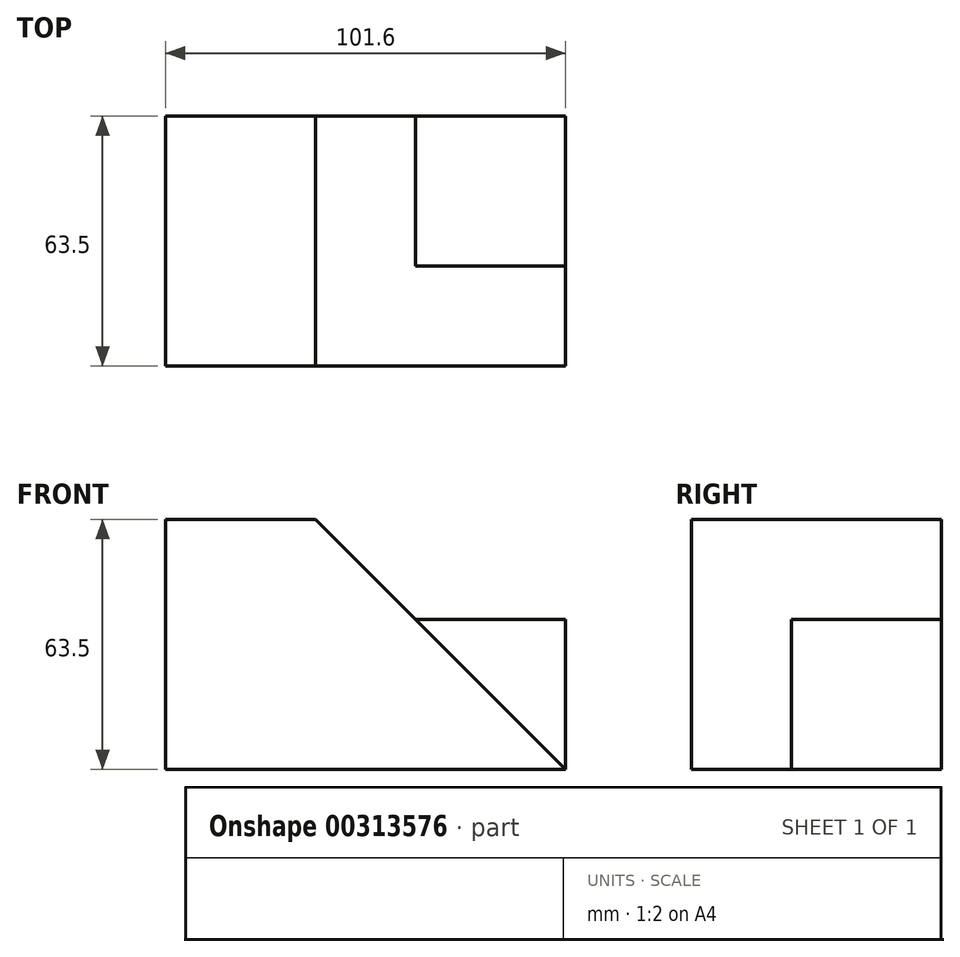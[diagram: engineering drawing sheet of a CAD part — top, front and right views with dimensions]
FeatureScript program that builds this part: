
annotation { "Feature Type Name" : "Feature", "Feature Type Description" : "" }
export const myFeature = defineFeature(function(context is Context, id is Id, definition is map)
    precondition{}
    {
        {
            var Q0;
            Q0=qCreatedBy(makeId("Front.planeOp"),FACE);
            var sketch = newSketch(context, id + "F0", { "sketchPlane" : qUnion([Q0])});
            skLineSegment(sketch, "E0", {"start": v(-12.7, 31.75) * mm, "end": v(-50.8, 31.75) * mm});
            skLineSegment(sketch, "E1", {"start": v(-50.8, 31.75) * mm, "end": v(-50.8, -31.75) * mm});
            skLineSegment(sketch, "E2", {"start": v(-50.8, -31.75) * mm, "end": v(50.8, -31.75) * mm});
            skLineSegment(sketch, "E3", {"start": v(50.8, -31.75) * mm, "end": v(-12.7, 31.75) * mm});
            skLineSegment(sketch, "E4", {"start": v(50.8, -31.75) * mm, "end": v(50.8, 6.35) * mm});
            skLineSegment(sketch, "E5", {"start": v(50.8, 6.35) * mm, "end": v(12.7, 6.35) * mm});
            skSolve(sketch);
        }
        {
            var Q0;
            {var subQ3=sQuery(id+"F0.wireOp",EDGE,"E0");Q0=makeQuery(id+"F0.imprint","IMPRINT",FACE,{"disambiguationData":[TD([[makeQuery(id+"F0.imprint","IMPRINT",EDGE,{"derivedFrom":subQ3}),1.0]])]});}
            extrude(context, id + "F1", {"entities" : qUnion([Q0]), "depth" : 63.5 * mm});
        }
        {
            var Q0;
            {var subQ0=sQuery(id+"F0.wireOp",EDGE,"E4");Q0=makeQuery(id+"F0.imprint","IMPRINT",FACE,{"disambiguationData":[TD([[makeQuery(id+"F0.imprint","IMPRINT",EDGE,{"derivedFrom":subQ0}),1.0]])]});}
            extrude(context, id + "F2", {"entities" : qUnion([Q0]), "operationType" : NewBodyOperationType.ADD, "depth" : 38.1 * mm});
        }
    });
